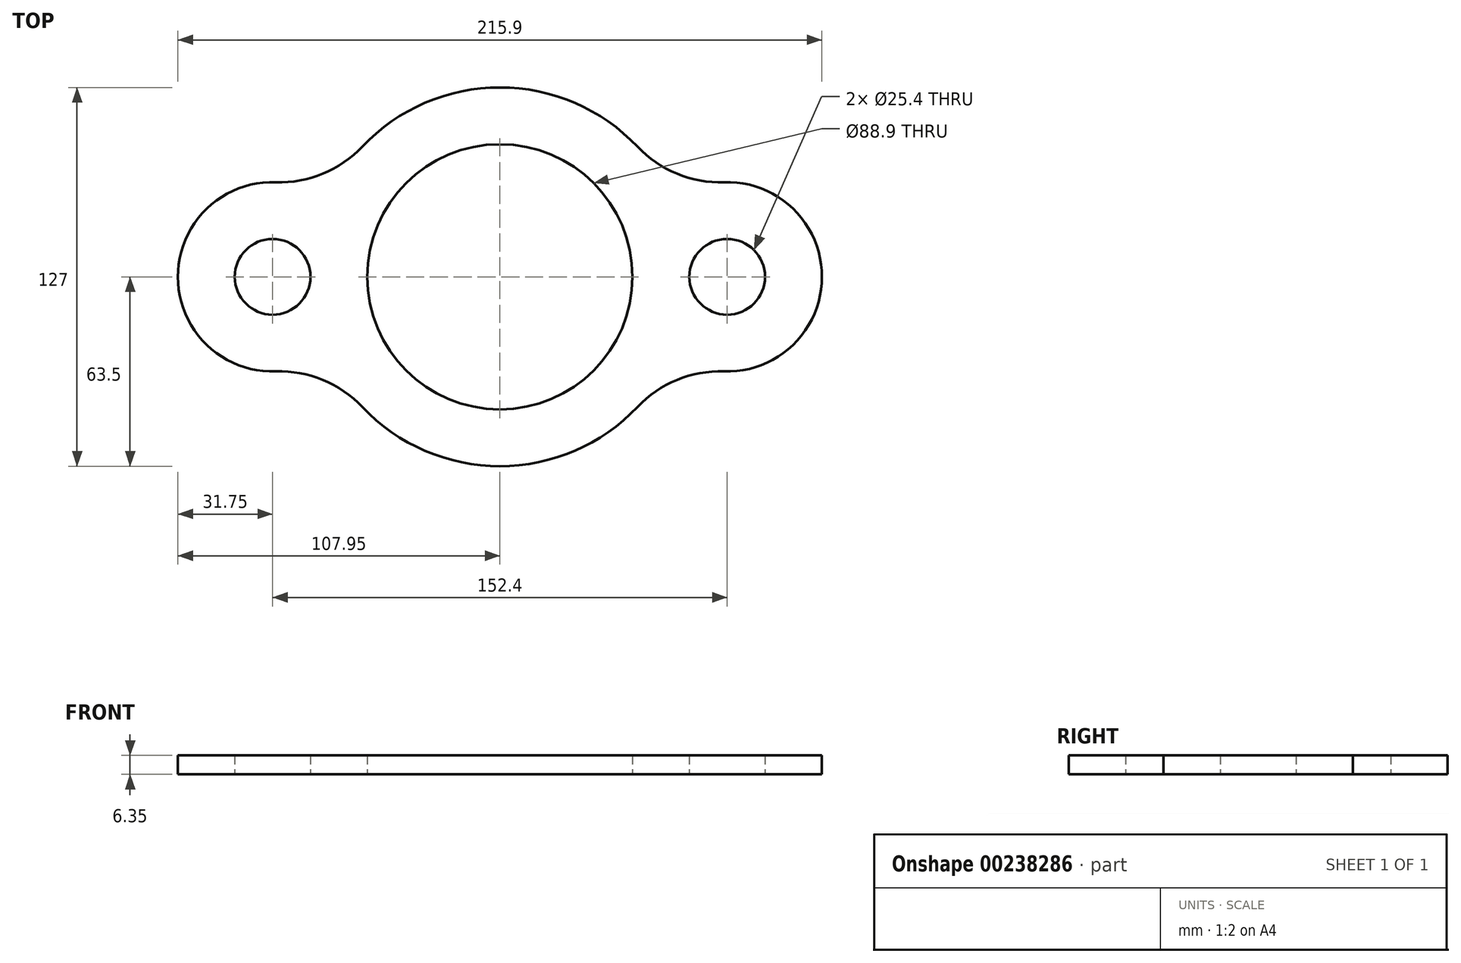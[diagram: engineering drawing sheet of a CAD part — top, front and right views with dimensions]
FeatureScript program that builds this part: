
annotation { "Feature Type Name" : "Feature", "Feature Type Description" : "" }
export const myFeature = defineFeature(function(context is Context, id is Id, definition is map)
    precondition{}
    {
        {
            var Q0;
            Q0=qCreatedBy(makeId("Top.planeOp"),FACE);
            var sketch = newSketch(context, id + "F0", { "sketchPlane" : qUnion([Q0])});
            skCircle(sketch, "E0", {"center": v(0, 0) * mm, "radius": 44.45 * mm});
            skCircle(sketch, "E1", {"center": v(-76.2, 0) * mm, "radius": 12.7 * mm});
            skCircle(sketch, "E2", {"center": v(76.2, 0) * mm, "radius": 12.7 * mm});
            skPoint(sketch, "E3", {"position": v(0, 31.75) * mm});
            skPoint(sketch, "E4", {"position": v(0, -31.75) * mm});
            skArc(sketch, "E5", {"start": v(75.12, -31.73) * mm, "mid": v(107.95, 0) * mm, "end": v(75.12, 31.73) * mm});
            skArc(sketch, "E6", {"start": v(-46.14, -43.63) * mm, "mid": v(0, -63.5) * mm, "end": v(46.14, -43.63) * mm});
            skArc(sketch, "E7", {"start": v(-75.12, 31.73) * mm, "mid": v(-107.95, 0) * mm, "end": v(-75.12, -31.73) * mm});
            skArc(sketch, "E8.trimOffspring", {"start": v(46.14, 43.63) * mm, "mid": v(0, 63.5) * mm, "end": v(-46.14, 43.63) * mm});
            skPoint(sketch, "E9.visualSharp", {"position": v(57.94, 25.98) * mm});
            skArc(sketch, "E9.filletArc", {"start": v(46.14, 43.63) * mm, "mid": v(59.35, 34.56) * mm, "end": v(75.12, 31.73) * mm});
            skPoint(sketch, "E10.visualSharp", {"position": v(57.94, -25.98) * mm});
            skArc(sketch, "E10.filletArc", {"start": v(75.12, -31.73) * mm, "mid": v(59.35, -34.56) * mm, "end": v(46.14, -43.63) * mm});
            skPoint(sketch, "E11.visualSharp", {"position": v(-57.94, -25.98) * mm});
            skArc(sketch, "E11.filletArc", {"start": v(-46.14, -43.63) * mm, "mid": v(-59.35, -34.56) * mm, "end": v(-75.12, -31.73) * mm});
            skPoint(sketch, "E12.visualSharp", {"position": v(-57.94, 25.98) * mm});
            skArc(sketch, "E12.filletArc", {"start": v(-75.12, 31.73) * mm, "mid": v(-59.35, 34.56) * mm, "end": v(-46.14, 43.63) * mm});
            skSolve(sketch);
        }
        {
            var Q0;
            Q0=makeQuery(id+"F0.imprint","IMPRINT",FACE,{"disambiguationData":[TD([[makeQuery(id+"F0.imprint","IMPRINT",EDGE,{"derivedFrom":sQuery(id+"F0.wireOp",EDGE,"E0")}),-1.0]])]});
            extrude(context, id + "F1", {"entities" : qUnion([Q0]), "depth" : 6.35 * mm});
        }
    });
